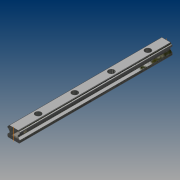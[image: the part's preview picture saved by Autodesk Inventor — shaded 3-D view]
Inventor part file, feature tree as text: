
AUTODESK INVENTOR PART (.ipt)
format: ipt  version: 2021 (Build 250183000, 183)  size: 286,208 bytes
history: native  units: mm
features: sketch x4, extrude x3, projected_geometry x3, other x2
ambient origin geometry x8: Origin, YZ Plane, XZ Plane, XY Plane, X Axis, Y Axis, Z Axis, Center Point
bodies: Solid1 (feature_tree)
feature tree (12):
  extrude  "Extrusion1"  Depth=250.0mm
  sketch  "Sketch2"  dims[d4=6.0mm d6=9.5mm d7=6.0mm]
  extrude  "Extrusion2"  Depth=9.5mm
  extrude  "Extrusion3"  Depth=9.5mm
  sketch  "Sketch3"  dims[d9=9.5mm d10=6.0mm d12=9.5mm d13=6.0mm]
  other  "Work Axis1"
  sketch  "Sketch4"  dims[d15=9.5mm d16=6.0mm d18=9.5mm d19=6.0mm d21=9.5mm d22=6.0mm d24=9.5mm d25=6.0mm d27=9.5mm d28=6.0mm d30=9.5mm d31=6.0mm d33=9.5mm d34=6.0mm d36=9.5mm d37=6.0mm d39=9.5mm d40=6.0mm d42=9.5mm d43=6.0mm d45=9.5mm d46=6.0mm d48=9.5mm d49=6.0mm d51=9.5mm d52=6.0mm d54=9.5mm d55=6.0mm d57=9.5mm d58=6.0mm d60=9.5mm d61=6.0mm d63=9.5mm d64=6.0mm d66=9.5mm d67=6.0mm d69=9.5mm d70=6.0mm d72=9.5mm d73=6.0mm d75=9.5mm d76=6.0mm d78=30.0mm d79=0.0mm d80=8.4mm d81=0.0mm d82=18.0mm d83=14.471441mm]
  other  "Work Axis2"
  sketch  "Sketch1"  dims[d0=250.0mm d1=0.0mm d3=9.5mm]
  projected_geometry  "Projected Loop1"
  projected_geometry  "Projected Loop2"
  projected_geometry  "Projected Loop3"
